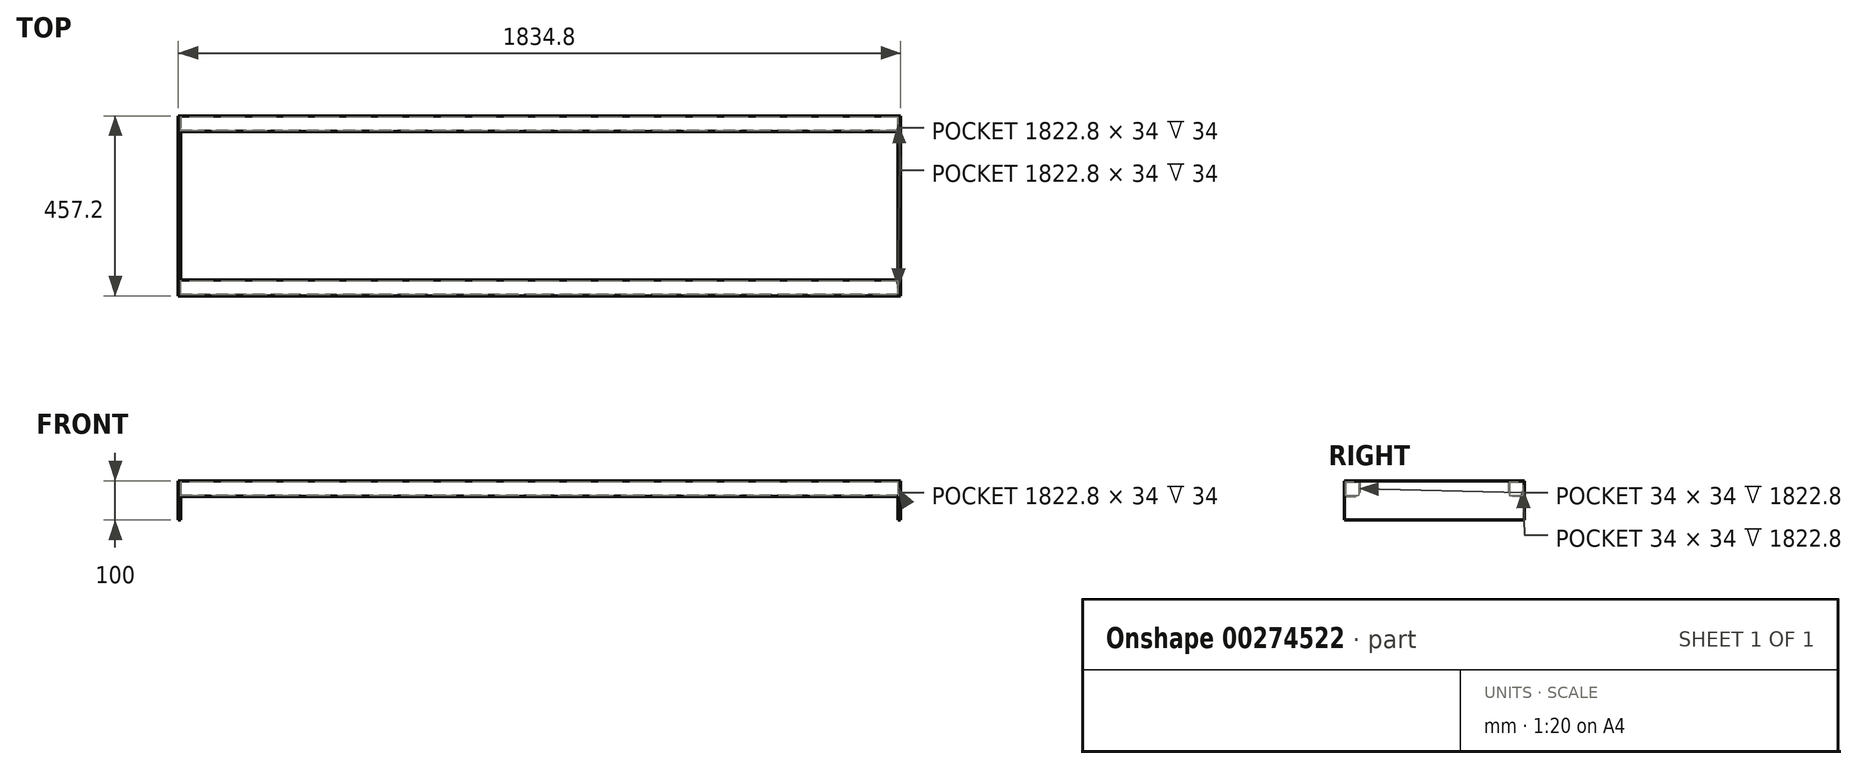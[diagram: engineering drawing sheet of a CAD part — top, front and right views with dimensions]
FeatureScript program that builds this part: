
annotation { "Feature Type Name" : "Feature", "Feature Type Description" : "" }
export const myFeature = defineFeature(function(context is Context, id is Id, definition is map)
    precondition{}
    {
        {
            var Q0;
            Q0=qCreatedBy(makeId("Right.planeOp"),FACE);
            var sketch = newSketch(context, id + "F0", { "sketchPlane" : qUnion([Q0])});
            skLineSegment(sketch, "E0.bottom", {"start": v(-21.7, 21.15) * mm, "end": v(18.3, 21.15) * mm});
            skLineSegment(sketch, "E0.top", {"start": v(-21.7, -18.85) * mm, "end": v(18.3, -18.85) * mm});
            skLineSegment(sketch, "E0.left", {"start": v(-21.7, 21.15) * mm, "end": v(-21.7, -18.85) * mm});
            skLineSegment(sketch, "E0.right", {"start": v(18.3, 21.15) * mm, "end": v(18.3, -18.85) * mm});
            skLineSegment(sketch, "E1.bottom", {"start": v(-18.7, 18.15) * mm, "end": v(15.3, 18.15) * mm});
            skLineSegment(sketch, "E1.top", {"start": v(-18.7, -15.85) * mm, "end": v(15.3, -15.85) * mm});
            skLineSegment(sketch, "E1.left", {"start": v(-18.7, 18.15) * mm, "end": v(-18.7, -15.85) * mm});
            skLineSegment(sketch, "E1.right", {"start": v(15.3, 18.15) * mm, "end": v(15.3, -15.85) * mm});
            skSolve(sketch);
        }
        {
            var Q0;
            Q0 = qSketchRegion(id + "F0", true);
            extrude(context, id + "F1", {"entities" : qUnion([Q0]), "depth" : 1828.8 * mm});
        }
        {
            var Q0;
            Q0=qCreatedBy(makeId("Right.planeOp"),FACE);
            var sketch = newSketch(context, id + "F2", { "sketchPlane" : qUnion([Q0])});
            skLineSegment(sketch, "E2.bottom", {"start": v(-21.7, 21.15) * mm, "end": v(435.5, 21.15) * mm});
            skLineSegment(sketch, "E2.top", {"start": v(-21.7, -78.85) * mm, "end": v(435.5, -78.85) * mm});
            skLineSegment(sketch, "E2.left", {"start": v(-21.7, 21.15) * mm, "end": v(-21.7, -78.85) * mm});
            skLineSegment(sketch, "E2.right", {"start": v(435.5, 21.15) * mm, "end": v(435.5, -78.85) * mm});
            skSolve(sketch);
        }
        {
            var Q0;
            Q0 = qSketchRegion(id + "F2", true);
            extrude(context, id + "F3", {"entities" : qUnion([Q0]), "operationType" : NewBodyOperationType.ADD, "depth" : 6 * mm});
        }
        {
            var Q0;
            {var subQ0=sQuery(id+"F2.wireOp",EDGE,"E2.top");var subQ1=sQuery(id+"F2.wireOp",EDGE,"E2.left");var subQ2=sQuery(id+"F2.wireOp",EDGE,"E2.bottom");var subQ3=sQuery(id+"F2.wireOp",EDGE,"E2.right");Q0=makeQuery(id+"F3.boolean.opBoolean","SPLIT",FACE,{"disambiguationData":[TD([makeQuery(id+"F1.opExtrude","SWEPT_FACE",FACE,{"disambiguationData":[OSD([sQuery(id+"F0.wireOp",EDGE,"E0.bottom")])]})])],"derivedFrom":makeQuery(id+"F3.opExtrude","CAP_FACE",FACE,{"disambiguationData":[OSD([subQ2,subQ0,subQ1,subQ3])],"isStart":false})});}
            var sketch = newSketch(context, id + "F4", { "sketchPlane" : qUnion([Q0])});
            skLineSegment(sketch, "E3.bottom", {"start": v(435.5, 21.15) * mm, "end": v(395.5, 21.15) * mm});
            skLineSegment(sketch, "E3.top", {"start": v(435.5, -18.85) * mm, "end": v(395.5, -18.85) * mm});
            skLineSegment(sketch, "E3.left", {"start": v(435.5, 21.15) * mm, "end": v(435.5, -18.85) * mm});
            skLineSegment(sketch, "E3.right", {"start": v(395.5, 21.15) * mm, "end": v(395.5, -18.85) * mm});
            skLineSegment(sketch, "E4.bottom", {"start": v(398.5, 18.15) * mm, "end": v(432.5, 18.15) * mm});
            skLineSegment(sketch, "E4.top", {"start": v(398.5, -15.85) * mm, "end": v(432.5, -15.85) * mm});
            skLineSegment(sketch, "E4.left", {"start": v(398.5, 18.15) * mm, "end": v(398.5, -15.85) * mm});
            skLineSegment(sketch, "E4.right", {"start": v(432.5, 18.15) * mm, "end": v(432.5, -15.85) * mm});
            skSolve(sketch);
        }
        {
            var Q0;
            Q0 = qSketchRegion(id + "F4", true);
            extrude(context, id + "F5", {"entities" : qUnion([Q0]), "operationType" : NewBodyOperationType.ADD, "depth" : 1828.8 * mm});
        }
        {
            var Q0;
            Q0=makeQuery(id+"F1.opExtrude","CAP_FACE",FACE,{"disambiguationData":[OSD([sQuery(id+"F0.wireOp",EDGE,"E0.bottom"),sQuery(id+"F0.wireOp",EDGE,"E0.top"),sQuery(id+"F0.wireOp",EDGE,"E0.left"),sQuery(id+"F0.wireOp",EDGE,"E0.right"),sQuery(id+"F0.wireOp",EDGE,"E1.bottom"),sQuery(id+"F0.wireOp",EDGE,"E1.top"),sQuery(id+"F0.wireOp",EDGE,"E1.left"),sQuery(id+"F0.wireOp",EDGE,"E1.right")])],"isStart":false});
            var sketch = newSketch(context, id + "F6", { "sketchPlane" : qUnion([Q0])});
            skLineSegment(sketch, "E5.bottom", {"start": v(-21.7, 21.15) * mm, "end": v(435.5, 21.15) * mm});
            skLineSegment(sketch, "E5.top", {"start": v(-21.7, -78.85) * mm, "end": v(435.5, -78.85) * mm});
            skLineSegment(sketch, "E5.left", {"start": v(-21.7, 21.15) * mm, "end": v(-21.7, -78.85) * mm});
            skLineSegment(sketch, "E5.right", {"start": v(435.5, 21.15) * mm, "end": v(435.5, -78.85) * mm});
            skSolve(sketch);
        }
        {
            var Q0;
            Q0 = qSketchRegion(id + "F6", true);
            extrude(context, id + "F7", {"entities" : qUnion([Q0]), "operationType" : NewBodyOperationType.ADD, "depth" : 6 * mm});
        }
    });
